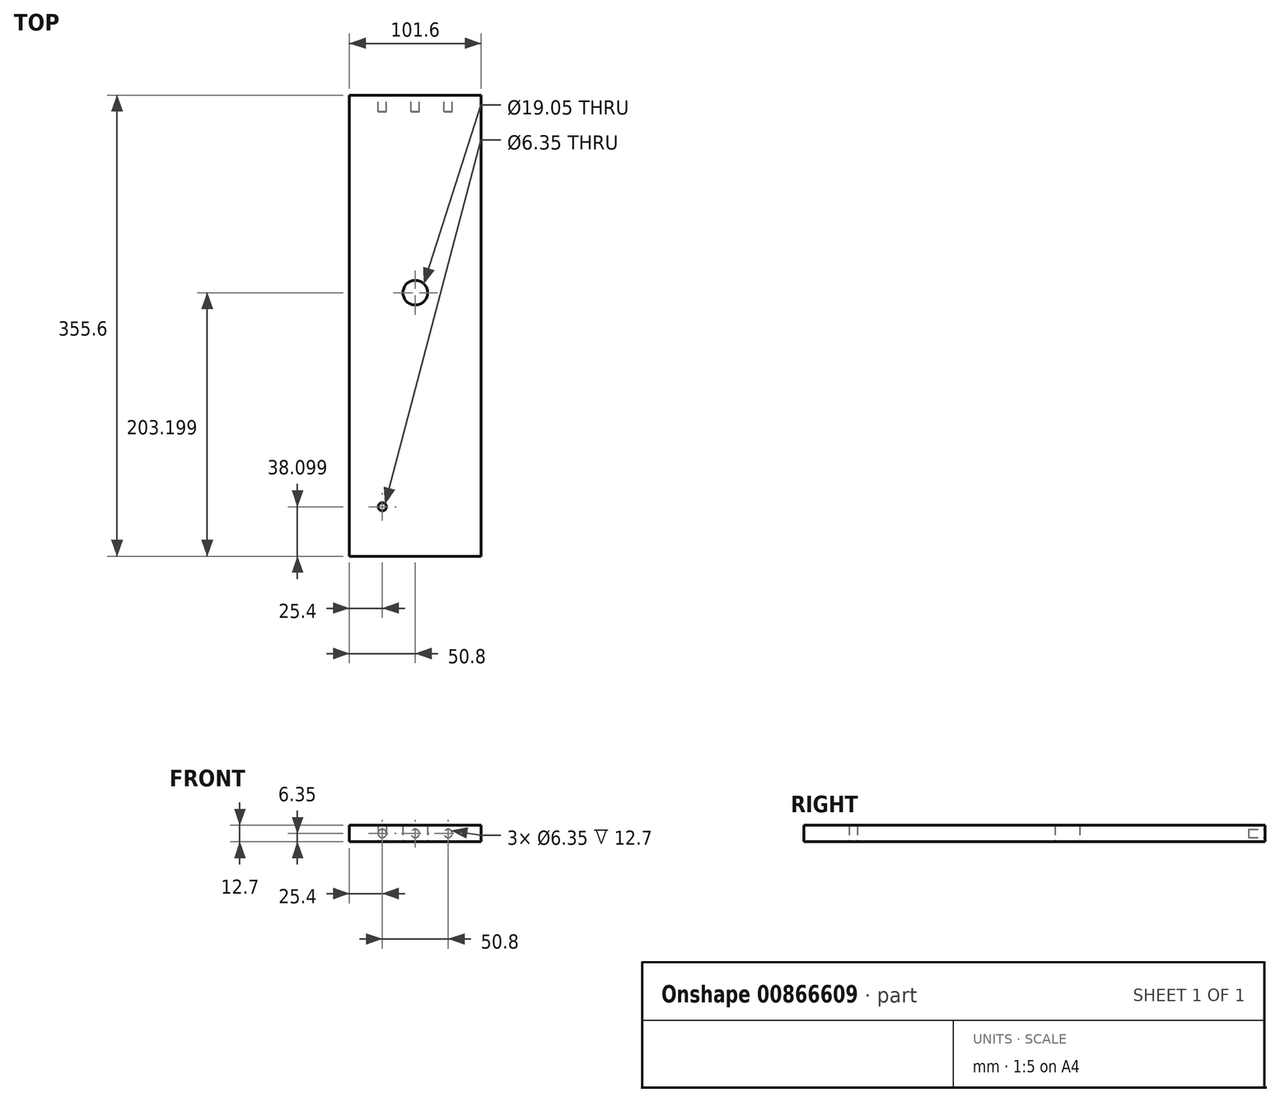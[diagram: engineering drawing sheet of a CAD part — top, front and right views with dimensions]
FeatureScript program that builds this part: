
annotation { "Feature Type Name" : "Feature", "Feature Type Description" : "" }
export const myFeature = defineFeature(function(context is Context, id is Id, definition is map)
    precondition{}
    {
        {
            var Q0;
            Q0=qCreatedBy(makeId("Top.planeOp"),FACE);
            var sketch = newSketch(context, id + "F0", { "sketchPlane" : qUnion([Q0])});
            skLineSegment(sketch, "E0.bottom", {"start": v(-50.8, 224.92) * mm, "end": v(50.8, 224.92) * mm});
            skLineSegment(sketch, "E0.top", {"start": v(-50.8, -130.68) * mm, "end": v(50.8, -130.68) * mm});
            skLineSegment(sketch, "E0.left", {"start": v(-50.8, 224.92) * mm, "end": v(-50.8, -130.68) * mm});
            skLineSegment(sketch, "E0.right", {"start": v(50.8, 224.92) * mm, "end": v(50.8, -130.68) * mm});
            skCircle(sketch, "E1", {"center": v(0, 72.52) * mm, "radius": 9.53 * mm});
            skCircle(sketch, "E2", {"center": v(-25.4, -92.58) * mm, "radius": 3.18 * mm});
            skSolve(sketch);
        }
        {
            var Q0;
            Q0=makeQuery(id+"F0.imprint","IMPRINT",FACE,{"disambiguationData":[TD([[makeQuery(id+"F0.imprint","IMPRINT",EDGE,{"derivedFrom":sQuery(id+"F0.wireOp",EDGE,"E0.bottom")}),-1.0]])]});
            extrude(context, id + "F1", {"entities" : qUnion([Q0]), "depth" : 12.7 * mm, "offsetDistance" : 25.4 * mm});
        }
        {
            var Q0;
            Q0=makeQuery(id+"F1.opExtrude","SWEPT_FACE",FACE,{"disambiguationData":[OSD([sQuery(id+"F0.wireOp",EDGE,"E0.bottom")])]});
            var sketch = newSketch(context, id + "F2", { "sketchPlane" : qUnion([Q0])});
            skCircle(sketch, "E3", {"center": v(-25.4, 6.35) * mm, "radius": 3.18 * mm});
            skCircle(sketch, "E4", {"center": v(0, 6.35) * mm, "radius": 3.18 * mm});
            skCircle(sketch, "E5", {"center": v(25.4, 6.35) * mm, "radius": 3.18 * mm});
            skSolve(sketch);
        }
        {
            var Q0;
            Q0=makeQuery(id+"F2.imprint","IMPRINT",FACE,{"disambiguationData":[TD([[makeQuery(id+"F2.imprint","IMPRINT",EDGE,{"derivedFrom":sQuery(id+"F2.wireOp",EDGE,"E3")}),1.0]])]});
            var Q1;
            Q1=makeQuery(id+"F2.imprint","IMPRINT",FACE,{"disambiguationData":[TD([[makeQuery(id+"F2.imprint","IMPRINT",EDGE,{"derivedFrom":sQuery(id+"F2.wireOp",EDGE,"E4")}),1.0]])]});
            var Q2;
            Q2=makeQuery(id+"F2.imprint","IMPRINT",FACE,{"disambiguationData":[TD([[makeQuery(id+"F2.imprint","IMPRINT",EDGE,{"derivedFrom":sQuery(id+"F2.wireOp",EDGE,"E5")}),1.0]])]});
            extrude(context, id + "F3", {"entities" : qUnion([Q0, Q1, Q2]), "operationType" : NewBodyOperationType.REMOVE, "oppositeDirection" : true, "depth" : 12.7 * mm, "offsetDistance" : 25.4 * mm});
        }
    });
